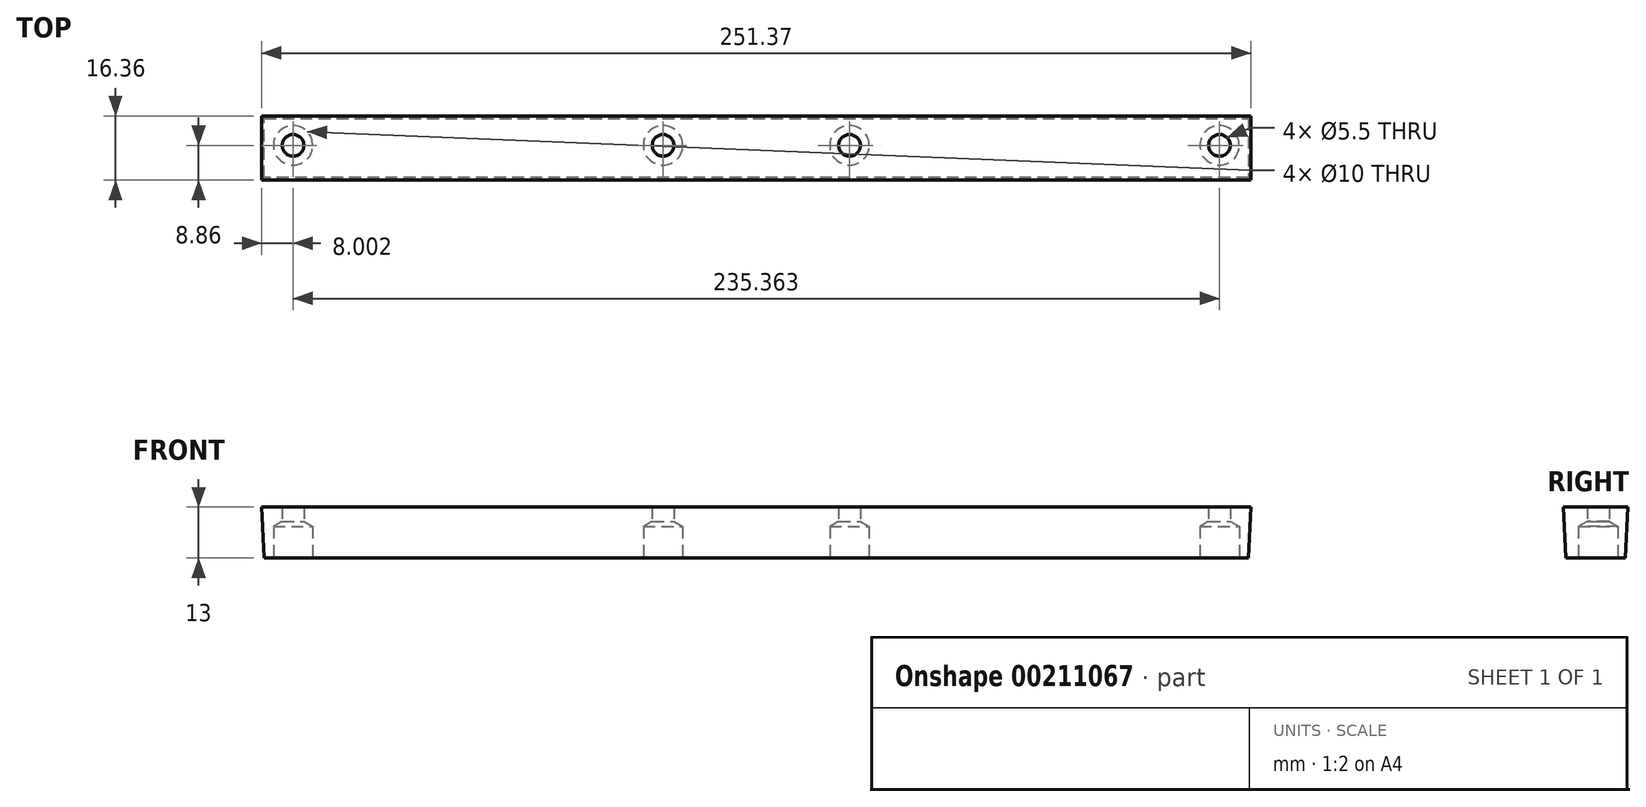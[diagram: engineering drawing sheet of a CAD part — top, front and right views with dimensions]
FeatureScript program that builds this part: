
annotation { "Feature Type Name" : "Feature", "Feature Type Description" : "" }
export const myFeature = defineFeature(function(context is Context, id is Id, definition is map)
    precondition{}
    {
        {
            var Q0;
            Q0=qCreatedBy(makeId("Top.planeOp"),FACE);
            var sketch = newSketch(context, id + "F0", { "sketchPlane" : qUnion([Q0])});
            skLineSegment(sketch, "E0.bottom", {"start": v(-138.73, 35.89) * mm, "end": v(111.27, 35.89) * mm});
            skLineSegment(sketch, "E0.top", {"start": v(-138.73, 20.89) * mm, "end": v(111.27, 20.89) * mm});
            skLineSegment(sketch, "E0.left", {"start": v(-138.73, 35.89) * mm, "end": v(-138.73, 20.89) * mm});
            skLineSegment(sketch, "E0.right", {"start": v(111.27, 35.89) * mm, "end": v(111.27, 20.89) * mm});
            skSolve(sketch);
        }
        {
            var Q0;
            Q0=makeQuery(id+"F0.imprint","IMPRINT",FACE,{"disambiguationData":[TD([[makeQuery(id+"F0.imprint","IMPRINT",EDGE,{"derivedFrom":sQuery(id+"F0.wireOp",EDGE,"E0.bottom")}),-1.0]])]});
            extrude(context, id + "F1", {"entities" : qUnion([Q0]), "depth" : 13 * mm, "hasDraft" : true, "draftAngle" : 3 * degree});
        }
        {
            var Q0;
            Q0=qCreatedBy(makeId("Top.planeOp"),FACE);
            var sketch = newSketch(context, id + "F2", { "sketchPlane" : qUnion([Q0])});
            skPoint(sketch, "E1", {"position": v(9.96, 29.07) * mm});
            skPoint(sketch, "E2", {"position": v(-37.4, 29.07) * mm});
            skPoint(sketch, "E3", {"position": v(-131.4, 29.07) * mm});
            skPoint(sketch, "E4", {"position": v(103.96, 29.07) * mm});
            skSolve(sketch);
        }
        {
            var Q0;
            Q0=sQuery(id+"F2.wireOp",VERTEX,"E3");
            var Q1;
            Q1=sQuery(id+"F2.wireOp",VERTEX,"E2");
            var Q2;
            Q2=sQuery(id+"F2.wireOp",VERTEX,"E1");
            var Q3;
            Q3=sQuery(id+"F2.wireOp",VERTEX,"E4");
            var Q4;
            Q4=makeQuery(id+"F1.opExtrude","SWEPT_BODY",BODY,{"disambiguationData":[OSD([sQuery(id+"F0.wireOp",EDGE,"E0.bottom"),sQuery(id+"F0.wireOp",EDGE,"E0.top"),sQuery(id+"F0.wireOp",EDGE,"E0.left"),sQuery(id+"F0.wireOp",EDGE,"E0.right")])]});
            hole(context, id + "F3", {"style" : HoleStyle.SIMPLE, "endStyle" : HoleEndStyle.THROUGH, "oppositeDirection" : true, "standardTappedOrClearance" : lookupTablePath({ "standard" : "ISO", "fit" : "Normal", "size" : "M5", "type" : "Clearance" }), "standardBlindInLast" : lookupTablePath({ "fit" : "Standard", "standard" : "ISO", "size" : "M5", "type" : "Clearance" }), "holeDiameter" : 5.5 * mm, "locations" : qUnion([Q0, Q1, Q2, Q3]), "scope" : qUnion([Q4]), "isTappedThrough" : true});
        }
        {
            var Q0;
            Q0=sQuery(id+"F2.wireOp",VERTEX,"E2");
            var Q1;
            Q1=sQuery(id+"F2.wireOp",VERTEX,"E1");
            var Q2;
            Q2=sQuery(id+"F2.wireOp",VERTEX,"E4");
            var Q3;
            Q3=sQuery(id+"F2.wireOp",VERTEX,"E3");
            var Q4;
            Q4=makeQuery(id+"F1.opExtrude","SWEPT_BODY",BODY,{"disambiguationData":[OSD([sQuery(id+"F0.wireOp",EDGE,"E0.bottom"),sQuery(id+"F0.wireOp",EDGE,"E0.top"),sQuery(id+"F0.wireOp",EDGE,"E0.left"),sQuery(id+"F0.wireOp",EDGE,"E0.right")])]});
            hole(context, id + "F4", {"style" : HoleStyle.SIMPLE, "endStyle" : HoleEndStyle.BLIND, "oppositeDirection" : true, "holeDiameter" : 10 * mm, "holeDepth" : 8 * mm, "locations" : qUnion([Q0, Q1, Q2, Q3]), "scope" : qUnion([Q4])});
        }
    });
